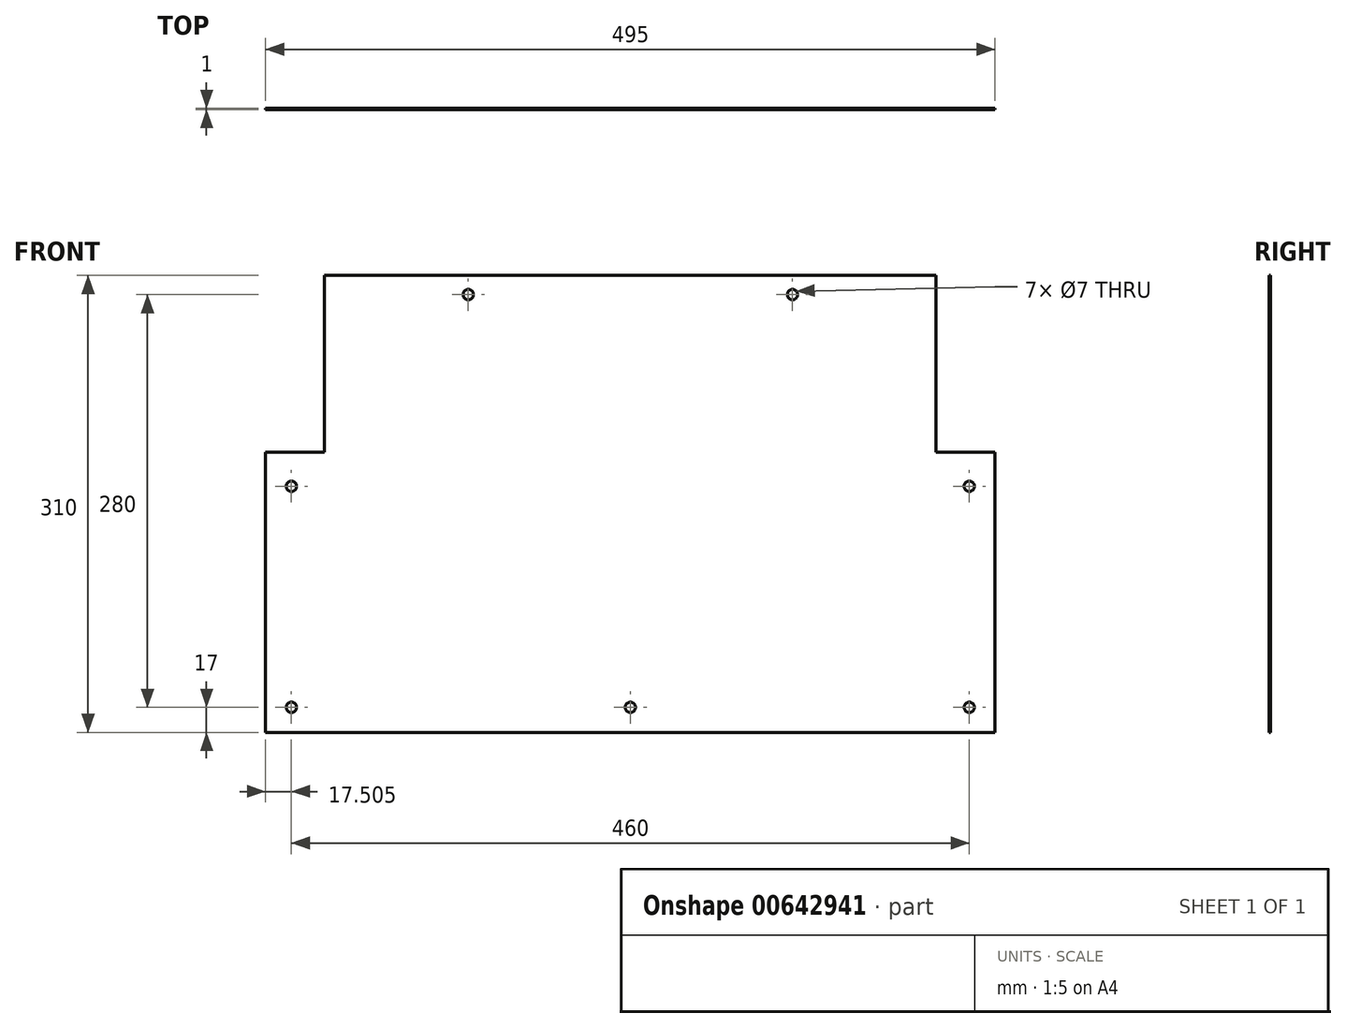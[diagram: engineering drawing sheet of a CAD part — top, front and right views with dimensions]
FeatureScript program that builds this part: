
annotation { "Feature Type Name" : "Feature", "Feature Type Description" : "" }
export const myFeature = defineFeature(function(context is Context, id is Id, definition is map)
    precondition{}
    {
        {
            var Q0;
            Q0=qCreatedBy(makeId("Front.planeOp"),FACE);
            var sketch = newSketch(context, id + "F0", { "sketchPlane" : qUnion([Q0])});
            skLineSegment(sketch, "E0", {"start": v(-61.15, 0) * mm, "end": v(433.85, 0) * mm});
            skLineSegment(sketch, "E1", {"start": v(433.85, 0) * mm, "end": v(433.85, 190) * mm});
            skLineSegment(sketch, "E2", {"start": v(-61.15, 0) * mm, "end": v(-61.15, 190) * mm});
            skPoint(sketch, "E3", {"position": v(186.35, 310) * mm});
            skPoint(sketch, "E3.positionSnap0", {"position": v(186.35, 0) * mm});
            skLineSegment(sketch, "E4", {"start": v(186.35, 310) * mm, "end": v(-21.15, 310) * mm});
            skLineSegment(sketch, "E5", {"start": v(186.35, 310) * mm, "end": v(393.85, 310) * mm});
            skLineSegment(sketch, "E6", {"start": v(393.85, 310) * mm, "end": v(393.85, 190) * mm});
            skLineSegment(sketch, "E7", {"start": v(393.85, 190) * mm, "end": v(433.85, 190) * mm});
            skLineSegment(sketch, "E8", {"start": v(-21.15, 310) * mm, "end": v(-21.15, 190) * mm});
            skLineSegment(sketch, "E9", {"start": v(-21.15, 190) * mm, "end": v(-61.15, 190) * mm});
            skCircle(sketch, "E10", {"center": v(-43.65, 17) * mm, "radius": 3.5 * mm});
            skCircle(sketch, "E11", {"center": v(186.35, 17) * mm, "radius": 3.5 * mm});
            skCircle(sketch, "E12", {"center": v(416.35, 17) * mm, "radius": 3.5 * mm});
            skCircle(sketch, "E13", {"center": v(416.35, 167) * mm, "radius": 3.5 * mm});
            skCircle(sketch, "E14", {"center": v(-43.65, 167) * mm, "radius": 3.5 * mm});
            skCircle(sketch, "E15", {"center": v(296.35, 297) * mm, "radius": 3.5 * mm});
            skCircle(sketch, "E16", {"center": v(76.35, 297) * mm, "radius": 3.5 * mm});
            skSolve(sketch);
        }
        {
            var Q0;
            Q0=makeQuery(id+"F0.imprint","IMPRINT",FACE,{"disambiguationData":[TD([[makeQuery(id+"F0.imprint","IMPRINT",EDGE,{"derivedFrom":sQuery(id+"F0.wireOp",EDGE,"E0")}),1.0]])]});
            extrude(context, id + "F1", {"entities" : qUnion([Q0]), "depth" : 1 * mm, "offsetDistance" : 25 * mm});
        }
    });
